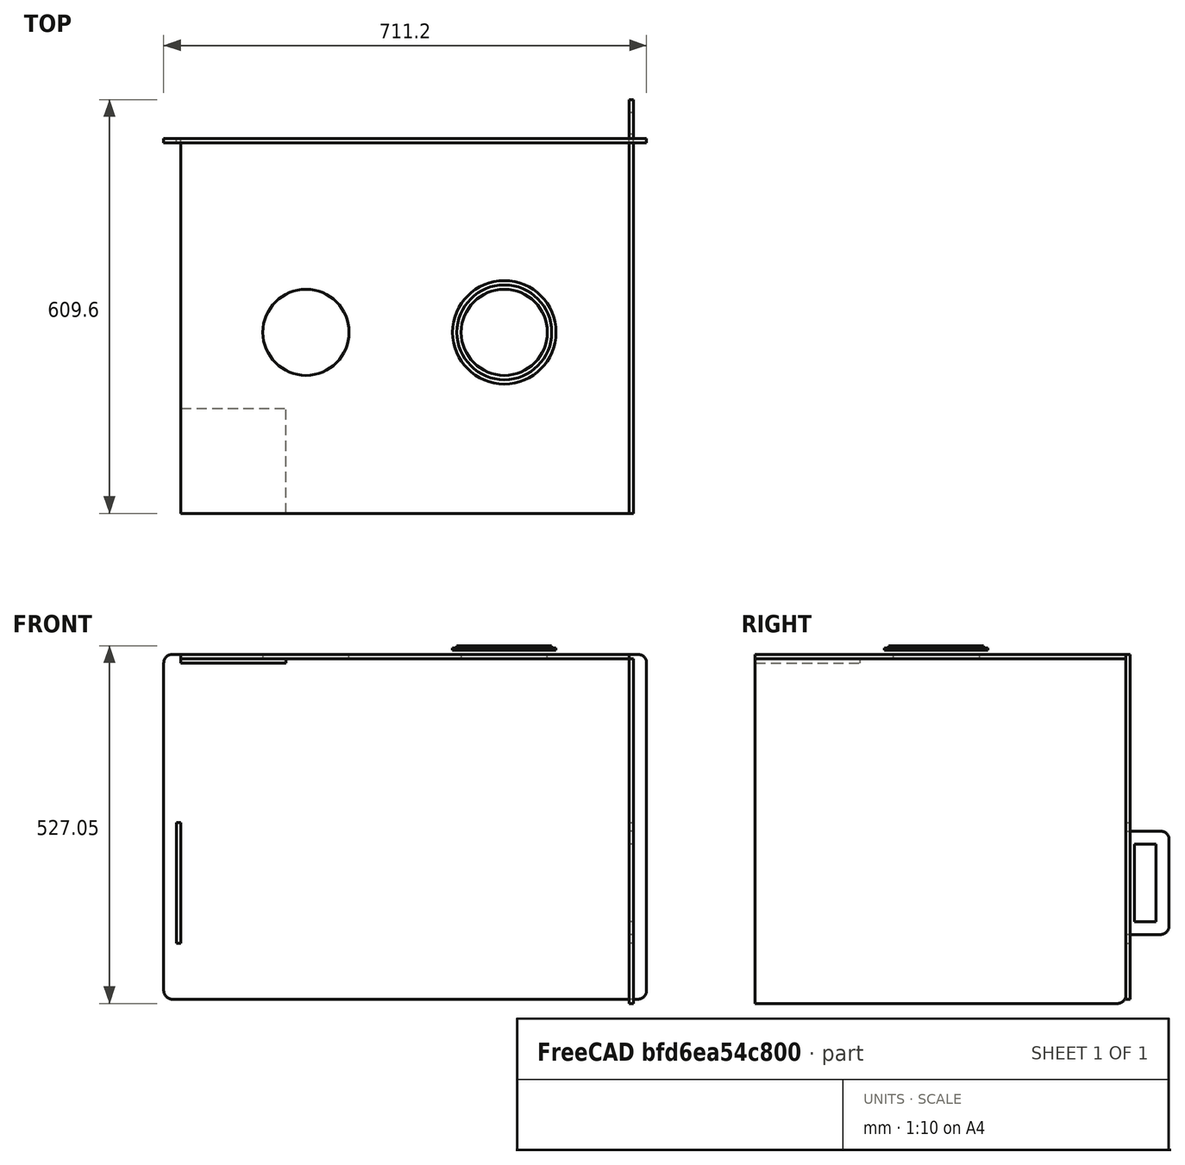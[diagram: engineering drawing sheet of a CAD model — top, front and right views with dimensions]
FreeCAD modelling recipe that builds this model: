
FCSTD DOCUMENT  (FreeCAD 0.19R20364 (Git))
Label: VS_folding_intubation_box
License: All rights reserved
LicenseURL: http://en.wikipedia.org/wiki/All_rights_reserved
objects: TechDraw::DrawViewDimension×28, Sketcher::SketchObject×7, PartDesign::Pad×6, Path::FeaturePython×6, PartDesign::Body×5, TechDraw::DrawSVGTemplate×5, TechDraw::DrawProjGroupItem×5, TechDraw::DrawPage×5, TechDraw::DrawProjGroup×4, TechDraw::DrawRichAnno×3, Part::FeaturePython×2, App::DocumentObjectGroup×2, App::FeaturePython×1, Path::FeatureCompoundPython×1, Part::Feature×1, TechDraw::DrawViewPart×1, Part::Part2DObjectPython×1
note: 31 computed .brp shape members not serialized (recipe doc carries the construction recipe); baked Part::Feature solids carry a one-line shape summary decoded from their .brp

FEATURE [Sketcher::SketchObject] Sketch
  MapMode = 5
  Support = -> [XY_Plane]
  sketch-geometry (7):
    g0: LineSegment StartX=0 StartY=0 StartZ=0 EndX=660.4 EndY=0 EndZ=0
    g1: LineSegment StartX=660.4 StartY=0 StartZ=0 EndX=660.4 EndY=546.1 EndZ=0
    g2: LineSegment StartX=660.4 StartY=546.1 StartZ=0 EndX=0 EndY=546.1 EndZ=0
    g3: LineSegment StartX=0 StartY=546.1 StartZ=0 EndX=0 EndY=0 EndZ=0
    g4: Circle CenterX=184.15 CenterY=266.7 CenterZ=0 NormalX=0 NormalY=0 NormalZ=1 AngleXU=0 Radius=63.5
    g5: Circle CenterX=476.25 CenterY=266.7 CenterZ=0 NormalX=0 NormalY=0 NormalZ=1 AngleXU=0 Radius=63.5
    g6: LineSegment [constr] StartX=660.4 StartY=266.7 StartZ=0 EndX=0 EndY=266.7 EndZ=0
  constraints (22):
    c: Coincident(g0,g1)
    c: Coincident(g1,g2)
    c: Coincident(g2,g3)
    c: Coincident(g3,g0)
    c: Horizontal(g0)
    c: Horizontal(g2)
    c: Vertical(g1)
    c: Vertical(g3)
    c: Coincident(g0,g-1)
    c: DistanceX(g2,g2) = 660.4
    c: DistanceY(g3,g3) = 546.1
    c: Diameter(g4) = 127
    c: Diameter(g5) = 127
    c: DistanceX(g4,g5) = 292.1
    c: DistanceX(g2,g4) = 184.15
    c: DistanceX(g5,g1) = 184.15
    c: PointOnObject(g6,g1)
    c: PointOnObject(g6,g3)
    c: Horizontal(g6)
    c: PointOnObject(g4,g6)
    c: PointOnObject(g5,g6)
    c: DistanceY(g0,g6) = 266.7
FEATURE [PartDesign::Pad] Pad
  Length = 6.35
  Length2 = 99.9998
  Profile = -> Sketch
  Type = 0
FEATURE [PartDesign::Body] Body  label="front"
  Group = -> [Sketch,Pad]
  Origin = -> Origin
  Tip = -> Pad
FEATURE [Sketcher::SketchObject] Sketch001
  MapMode = 5
  Support = -> [XY_Plane001]
  sketch-geometry (16):
    g0: LineSegment StartX=0 StartY=0 StartZ=0 EndX=-508 EndY=0 EndZ=0
    g1: LineSegment StartX=-508 StartY=0 StartZ=0 EndX=-508 EndY=533.4 EndZ=0
    g2: LineSegment StartX=-495.3 StartY=546.1 StartZ=0 EndX=-406.4 EndY=546.1 EndZ=0
    g3: LineSegment StartX=0 StartY=546.1 StartZ=0 EndX=0 EndY=0 EndZ=0
    g4: ArcOfCircle CenterX=-495.3 CenterY=533.4 CenterZ=0 NormalX=0 NormalY=0 NormalZ=1 AngleXU=0 Radius=12.7 StartAngle=1.5708 EndAngle=3.14159
    g5: LineSegment StartX=-254 StartY=546.1 StartZ=0 EndX=-254 EndY=596.9 EndZ=0
    g6: LineSegment StartX=-266.7 StartY=609.6 StartZ=0 EndX=-393.7 EndY=609.6 EndZ=0
    g7: LineSegment StartX=-406.4 StartY=596.9 StartZ=0 EndX=-406.4 EndY=546.1 EndZ=0
    g8: LineSegment StartX=-387.35 StartY=590.55 StartZ=0 EndX=-273.05 EndY=590.55 EndZ=0
    g9: LineSegment StartX=-273.05 StartY=590.55 StartZ=0 EndX=-273.05 EndY=558.8 EndZ=0
    g10: LineSegment StartX=-273.05 StartY=558.8 StartZ=0 EndX=-387.35 EndY=558.8 EndZ=0
    g11: LineSegment StartX=-387.35 StartY=558.8 StartZ=0 EndX=-387.35 EndY=590.55 EndZ=0
    g12: LineSegment StartX=-254 StartY=546.1 StartZ=0 EndX=0 EndY=546.1 EndZ=0
    g13: GeomPoint X=-330.2 Y=609.6 Z=0
    g14: ArcOfCircle CenterX=-266.7 CenterY=596.9 CenterZ=0 NormalX=0 NormalY=0 NormalZ=1 AngleXU=0 Radius=12.7 StartAngle=0 EndAngle=1.5708
    g15: ArcOfCircle CenterX=-393.7 CenterY=596.9 CenterZ=0 NormalX=0 NormalY=0 NormalZ=1 AngleXU=0 Radius=12.7 StartAngle=1.5708 EndAngle=3.14159
  constraints (42):
    c: Coincident(g0,g1)
    c: Coincident(g12,g3)
    c: Coincident(g3,g0)
    c: Horizontal(g0)
    c: Horizontal(g2)
    c: Vertical(g1)
    c: Vertical(g3)
    c: Coincident(g0,g-1)
    c: Tangent(g1,g4) = 1.5708
    c: Tangent(g2,g4) = 1.5708
    c: Radius(g4) = 12.7
    c: DistanceX(g0,g0) = 508
    c: DistanceY(g0,g12) = 546.1
    c: Vertical(g5)
    c: Horizontal(g6)
    c: Vertical(g7)
    c: Coincident(g8,g9)
    c: Coincident(g9,g10)
    c: Coincident(g10,g11)
    c: Coincident(g11,g8)
    c: Horizontal(g8)
    c: Horizontal(g10)
    c: Vertical(g9)
    c: Vertical(g11)
    c: Coincident(g2,g7)
    c: Coincident(g12,g5)
    c: Tangent(g2,g12)
    c: DistanceY(g11,g11) = 31.75
    c: DistanceX(g8,g8) = 114.3
    c: DistanceX(g13,g3) = 330.2
    c: Tangent(g6,g14) = -1.5708
    c: Tangent(g5,g14) = -1.5708
    c: DistanceX(g9,g5) = 19.05
    c: Radius(g14) = 12.7
    c: Tangent(g7,g15) = -1.5708
    c: Tangent(g6,g15) = -1.5708
    c: Radius(g15) = 12.7
    c: DistanceX(g2,g10) = 19.05
    c: DistanceY(g2,g6) = 63.5
    c: DistanceY(g0,g6) = 609.6
    c: Symmetric(g6,g6,g13)
    c: DistanceY(g8,g6) = 19.05
FEATURE [PartDesign::Pad] Pad001
  Length = 6.35
  Length2 = 99.9998
  Profile = -> Sketch001
  Type = 0
FEATURE [PartDesign::Body] Body001  label="left"
  Group = -> [Sketch001,Pad001]
  Origin = -> Origin001
  Placement = pos=(0,0,0) rot=(0,-1,0;1.5708rad)
  Tip = -> Pad001
FEATURE [Sketcher::SketchObject] Sketch002
  MapMode = 5
  Support = -> [XY_Plane002]
  sketch-geometry (19):
    g0: LineSegment StartX=12.7 StartY=-6.35 StartZ=0 EndX=698.5 EndY=-6.35 EndZ=0
    g1: LineSegment StartX=711.2 StartY=6.35 StartZ=0 EndX=711.2 EndY=488.95 EndZ=0
    g2: LineSegment StartX=698.5 StartY=501.65 StartZ=0 EndX=12.7 EndY=501.65 EndZ=0
    g3: LineSegment StartX=0 StartY=488.95 StartZ=0 EndX=0 EndY=6.35 EndZ=0
    g4: LineSegment StartX=692.15 StartY=419.1 StartZ=0 EndX=685.8 EndY=419.1 EndZ=0
    g5: LineSegment StartX=685.8 StartY=419.1 StartZ=0 EndX=685.8 EndY=241.3 EndZ=0
    g6: LineSegment StartX=685.8 StartY=241.3 StartZ=0 EndX=692.15 EndY=241.3 EndZ=0
    g7: LineSegment StartX=692.15 StartY=241.3 StartZ=0 EndX=692.15 EndY=419.1 EndZ=0
    g8: GeomPoint X=692.15 Y=330.2 Z=0
    g9: ArcOfCircle CenterX=698.5 CenterY=488.95 CenterZ=0 NormalX=0 NormalY=0 NormalZ=1 AngleXU=0 Radius=12.7 StartAngle=-9e-16 EndAngle=1.5708
    g10: LineSegment StartX=25.4 StartY=419.1 StartZ=0 EndX=19.05 EndY=419.1 EndZ=0
    g11: LineSegment StartX=19.05 StartY=419.1 StartZ=0 EndX=19.05 EndY=241.3 EndZ=0
    g12: LineSegment StartX=19.05 StartY=241.3 StartZ=0 EndX=25.4 EndY=241.3 EndZ=0
    g13: LineSegment StartX=25.4 StartY=241.3 StartZ=0 EndX=25.4 EndY=419.1 EndZ=0
    g14: GeomPoint X=25.4 Y=330.2 Z=0
    g15: ArcOfCircle CenterX=12.7 CenterY=488.95 CenterZ=0 NormalX=0 NormalY=0 NormalZ=1 AngleXU=0 Radius=12.7 StartAngle=1.5708 EndAngle=3.14159
    g16: ArcOfCircle CenterX=698.5 CenterY=6.35 CenterZ=0 NormalX=0 NormalY=0 NormalZ=1 AngleXU=0 Radius=12.7 StartAngle=4.71239 EndAngle=6.28319
    g17: ArcOfCircle CenterX=12.7 CenterY=6.35 CenterZ=0 NormalX=0 NormalY=0 NormalZ=1 AngleXU=0 Radius=12.7 StartAngle=3.14159 EndAngle=4.71239
    g18: LineSegment [constr] StartX=-26.162 StartY=330.2 StartZ=0 EndX=801.937 EndY=330.2 EndZ=0
  constraints (48):
    c: Horizontal(g0)
    c: Horizontal(g2)
    c: Vertical(g1)
    c: Coincident(g4,g5)
    c: Coincident(g5,g6)
    c: Coincident(g7,g4)
    c: Horizontal(g4)
    c: Horizontal(g6)
    c: Vertical(g5)
    c: Vertical(g7)
    c: DistanceX(g6,g6) = 6.35
    c: Symmetric(g4,g6,g8)
    c: DistanceY(g7,g7) = 177.8
    c: Tangent(g2,g9) = -1.5708
    c: Tangent(g1,g9) = -1.5708
    c: Radius(g9) = 12.7
    c: Coincident(g10,g11)
    c: Coincident(g11,g12)
    c: Coincident(g13,g10)
    c: Horizontal(g10)
    c: Horizontal(g12)
    c: Vertical(g11)
    c: Vertical(g13)
    c: Equal(g6,g12) = 6.35
    c: Symmetric(g10,g12,g14)
    c: Equal(g7,g13) = 177.8
    c: DistanceX(g-1,g12) = 25.4
    c: Tangent(g3,g15) = -1.5708
    c: Tangent(g2,g15) = -1.5708
    c: Radius(g15) = 12.7
    c: Tangent(g0,g16) = -1.5708
    c: Tangent(g1,g16) = -1.5708
    c: DistanceY(g0,g2) = 508
    c: DistanceX(g5,g1) = 25.4
    c: Radius(g16) = 12.7
    c: DistanceX(g3,g1) = 711.2
    c: Tangent(g0,g17) = -1.5708
    c: Tangent(g3,g17) = -1.5708
    c: Radius(g17) = 12.7
    c: DistanceY(g0,g-1) = 6.35
    c: Horizontal(g18)
    c: PointOnObject(g8,g18)
    c: DistanceY(g0,g18) = 336.55
    c: Coincident(g7,g6)
    c: Coincident(g13,g12)
    c: PointOnObject(g14,g18)
    c: Tangent(g3,g-2)
    c: DistanceX(g18,g-1) = 26.162
FEATURE [PartDesign::Pad] Pad002
  Length = 6.35
  Length2 = 99.9998
  Profile = -> Sketch002
  Type = 0
FEATURE [PartDesign::Body] Body002  label="top"
  Group = -> [Sketch002,Pad002]
  Origin = -> Origin002
  Placement = pos=(-25.4,546.1,0) rot=(-1,0,0;1.5708rad)
  Tip = -> Pad002
FEATURE [Sketcher::SketchObject] Sketch003
  MapMode = 5
  Support = -> [XY_Plane003]
  sketch-geometry (2):
    g0: Circle CenterX=0 CenterY=0 CenterZ=0 NormalX=0 NormalY=0 NormalZ=1 AngleXU=0 Radius=63.5
    g1: Circle CenterX=0 CenterY=0 CenterZ=0 NormalX=0 NormalY=0 NormalZ=1 AngleXU=0 Radius=76.2
  constraints (4):
    c: Coincident(g0,g-1)
    c: Coincident(g1,g0)
    c: Diameter(g0) = 127
    c: Diameter(g1) = 152.4
FEATURE [PartDesign::Pad] Pad003
  Length = 3.175
  Length2 = 99.9998
  Profile = -> Sketch003
  Type = 0
FEATURE [Sketcher::SketchObject] Sketch004
  ExternalGeometry = -> [Pad003]
  MapMode = 5
  Placement = pos=(0,0,3.175) rot=(0,0,1;0rad)
  Support = -> [Pad003]
  sketch-geometry (2):
    g0: Circle CenterX=0 CenterY=0 CenterZ=0 NormalX=0 NormalY=0 NormalZ=1 AngleXU=0 Radius=69.85
    g1: Circle CenterX=0 CenterY=0 CenterZ=0 NormalX=0 NormalY=0 NormalZ=1 AngleXU=0 Radius=63.5
  constraints (4):
    c: Coincident(g0,g-1)
    c: Diameter(g0) = 139.7
    c: Coincident(g1,g0)
    c: Diameter(g1) = 127
FEATURE [PartDesign::Pad] Pad004
  BaseFeature = -> Pad003
  Length = 3.175
  Length2 = 99.9998
  Profile = -> Sketch004
  Type = 0
FEATURE [PartDesign::Body] Body003  label="glove_holder"
  Group = -> [Sketch003,Pad003,Sketch004,Pad004]
  Origin = -> Origin003
  Placement = pos=(184.15,266.7,12.7) rot=(1,0,0;0rad)
  Tip = -> Pad004
FEATURE [App::FeaturePython] SetupSheet  # Path/CAM operation (typed FeaturePython)
  ClearanceHeightExpression = OpStockZMax+SetupSheet.ClearanceHeightOffset
  ClearanceHeightOffset = 5.0038
  CoolantMode = 0
  CoolantModes = None | Flood | Mist
  FinalDepthExpression = OpFinalDepth
  HorizRapid = 0
  SafeHeightExpression = OpStockZMax+SetupSheet.SafeHeightOffset
  SafeHeightOffset = 2.9972
  StartDepthExpression = OpStartDepth
  StepDownExpression = OpToolDiameter
  VertRapid = 0
FEATURE [Part::FeaturePython] Clone  label="Model-glove_holder"  # Draft clone (typed FeaturePython)
  AttacherType = Attacher::AttachEngine3D
  Fuse = false
  Objects = -> [Body003]
  PathResource = Model
  Placement = pos=(76.9435,77.1288,-6.35) rot=(1,0,0;0rad)
  Scale = (1,1,1)
FEATURE [App::DocumentObjectGroup] Model
  Group = -> [Clone]
FEATURE [Path::FeaturePython] Default_Tool  label="Default Tool"  # Path/CAM operation (typed FeaturePython)
  HorizFeed = 0
  HorizRapid = 0
  SpindleDir = 0
  SpindleSpeed = 0
  ToolNumber = 1
  VertFeed = 0
  VertRapid = 0
  expr: VertRapid = SetupSheet.VertRapid
  expr: HorizRapid = SetupSheet.HorizRapid
FEATURE [Part::FeaturePython] Stock  # WARN: FeaturePython — macro-defined, semantics opaque (R4)
  Base = -> Model
  ExtXneg = 0.9906
  ExtXpos = 0.9906
  ExtYneg = 0.9906
  ExtYpos = 0.9906
  ExtZneg = 0
  ExtZpos = 0
  Placement = pos=(0.9906,0.9906,-6.35) rot=(0,0,1;0rad)
  StockType = FromBase
FEATURE [Path::FeaturePython] T5__1_8_endmill  label="T5: 1/8 endmill"  # Path/CAM operation (typed FeaturePython)
  HorizFeed = 19.05
  HorizRapid = 0
  SpindleDir = 0
  SpindleSpeed = 20000
  ToolNumber = 5
  VertFeed = 8.46667
  VertRapid = 0
  expr: VertRapid = SetupSheet.VertRapid
  expr: HorizRapid = SetupSheet.HorizRapid
FEATURE [Path::FeaturePython] Profile_Edges  # Path/CAM operation (typed FeaturePython)
  Active = true
  AreaParams:
    Tolerance = 1e-07
    FitArcs = True
    Simplify = False
    CleanDistance = 0.0
    Accuracy = 0.01
    Unit = 1.0
    MinArcPoints = 4
    MaxArcPoints = 100
    ClipperScale = 10000000.0
    Fill = 0
    Coplanar = 0
    Reorient = True
    Outline = False
    Explode = False
    OpenMode = 0
    Deflection = 0.01
    SubjectFill = 0
    ClipFill = 0
    Offset = -1.5875
    ExtraPass = 0
    Stepover = 0.0
    LastStepover = 0.0
    JoinType = 0
    EndType = 0
    MiterLimit = 2.0
    RoundPrecision = 0.0
    PocketMode = 0
    ToolRadius = 1.0
    PocketExtraOffset = 0.0
    PocketStepover = 0.0
    PocketLastStepover = 0.0
    FromCenter = False
    Angle = 45.0
    AngleShift = 0.0
    Shift = 0.0
    Thicken = False
    SectionCount = -1
    Stepdown = 1.0
    SectionOffset = 0.0
    SectionTolerance = 1e-06
    SectionMode = 2
    Project = False
  Base = -> [Clone]
  ClearanceHeight = 5.0038
  CoolantMode = None
  Direction = 0
  EnableRotation = 0
  FinalDepth = -6.4008
  JoinType = 0
  MiterLimit = 0.1
  OffsetExtra = 0
  OpFinalDepth = -6.35
  OpStartDepth = 0
  OpStockZMax = 0
  OpStockZMin = -6.35
  OpToolDiameter = 3.175
  PathParams = {'orientation': 1, 'feedrate': 19.05, 'feedrate_v': 8.46667, 'verbose': True, 'resume_height': 2.9972, 'retraction': 5.0038, 'return_end': True, 'preamble': False}
  SafeHeight = 2.9972
  Side = 1
  StartDepth = 0
  StartPoint = (0,0,0)
  StepDown = 3.2004
  ToolController = -> T5__1_8_endmill
  UseComp = true
  UseStartPoint = false
  expr: StartDepth = OpStartDepth
  expr: FinalDepth = -0.252in
  expr: StepDown = 0.126in
  expr: SafeHeight = OpStockZMax + SetupSheet.SafeHeightOffset
  expr: ClearanceHeight = OpStockZMax + SetupSheet.ClearanceHeightOffset
FEATURE [Path::FeaturePython] Pocket_Shape  # Path/CAM operation (typed FeaturePython)
  Active = true
  AreaParams:
    Tolerance = 1e-07
    FitArcs = True
    Simplify = False
    CleanDistance = 0.0
    Accuracy = 0.01
    Unit = 1.0
    MinArcPoints = 4
    MaxArcPoints = 100
    ClipperScale = 10000000.0
    Fill = 0
    Coplanar = 0
    Reorient = True
    Outline = False
    Explode = False
    OpenMode = 0
    Deflection = 0.01
    SubjectFill = 0
    ClipFill = 0
    Offset = 0.0
    ExtraPass = 0
    Stepover = 0.0
    LastStepover = 0.0
    JoinType = 0
    EndType = 0
    MiterLimit = 2.0
    RoundPrecision = 0.0
    PocketMode = 3
    ToolRadius = 1.5875
    PocketExtraOffset = 0.254
    PocketStepover = 2.54
    PocketLastStepover = 0.0
    FromCenter = True
    Angle = 45.0
    AngleShift = 0.0
    Shift = 0.0
    Thicken = False
    SectionCount = -1
    Stepdown = 1.0
    SectionOffset = 0.0
    SectionTolerance = 1e-06
    SectionMode = 2
    Project = False
  AttemptInverseAngle = true
  Base = -> [Clone]
  ClearanceHeight = 5.0038
  CoolantMode = None
  CutMode = 0
  EnableRotation = 0
  ExtensionCorners = true
  ExtensionLengthDefault = 1.5875
  ExtraOffset = 0.254
  FinalDepth = -3.175
  FinishDepth = 0
  InverseAngle = false
  KeepToolDown = false
  LimitDepthToFace = true
  MinTravel = false
  OffsetPattern = 2
  OpFinalDepth = -3.175
  OpStartDepth = 0
  OpStockZMax = 0
  OpStockZMin = -6.35
  OpToolDiameter = 3.175
  PathParams = {'orientation': 1, 'feedrate': 19.05, 'feedrate_v': 8.46667, 'verbose': True, 'resume_height': 2.9972, 'retraction': 5.0038, 'return_end': True, 'preamble': False}
  ReverseDirection = false
  SafeHeight = 2.9972
  StartAt = 0
  StartDepth = 0
  StartPoint = (0,0,0)
  StepDown = 3.175
  StepOver = 80
  ToolController = -> T5__1_8_endmill
  UseOutline = false
  UseStartPoint = false
  ZigZagAngle = 45
  expr: StartDepth = OpStartDepth
  expr: FinalDepth = OpFinalDepth
  expr: StepDown = OpToolDiameter
  expr: SafeHeight = OpStockZMax + SetupSheet.SafeHeightOffset
  expr: ClearanceHeight = OpStockZMax + SetupSheet.ClearanceHeightOffset
  expr: ExtensionLengthDefault = OpToolDiameter / 2
FEATURE [Path::FeaturePython] Contour  # Path/CAM operation (typed FeaturePython)
  Active = true
  AreaParams:
    Tolerance = 1e-07
    FitArcs = True
    Simplify = False
    CleanDistance = 0.0
    Accuracy = 0.01
    Unit = 1.0
    MinArcPoints = 4
    MaxArcPoints = 100
    ClipperScale = 10000000.0
    Fill = 0
    Coplanar = 2
    Reorient = True
    Outline = False
    Explode = False
    OpenMode = 0
    Deflection = 0.01
    SubjectFill = 0
    ClipFill = 0
    Offset = 1.5875
    ExtraPass = 0
    Stepover = 0.0
    LastStepover = 0.0
    JoinType = 0
    EndType = 0
    MiterLimit = 2.0
    RoundPrecision = 0.0
    PocketMode = 0
    ToolRadius = 1.0
    PocketExtraOffset = 0.0
    PocketStepover = 0.0
    PocketLastStepover = 0.0
    FromCenter = False
    Angle = 45.0
    AngleShift = 0.0
    Shift = 0.0
    Thicken = False
    SectionCount = -1
    Stepdown = 1.0
    SectionOffset = 0.0
    SectionTolerance = 1e-06
    SectionMode = 2
    Project = False
  ClearanceHeight = 5.0038
  CoolantMode = None
  Direction = 0
  EnableRotation = 0
  FinalDepth = -6.4008
  JoinType = 0
  MiterLimit = 0.1
  OffsetExtra = 0
  OpFinalDepth = -6.35
  OpStartDepth = 0
  OpStockZMax = 0
  OpStockZMin = -6.35
  OpToolDiameter = 3.175
  PathParams = {'orientation': 1, 'feedrate': 19.05, 'feedrate_v': 8.46667, 'verbose': True, 'resume_height': 2.9972, 'retraction': 5.0038, 'return_end': True, 'preamble': False}
  SafeHeight = 2.9972
  Side = 0
  StartDepth = 0
  StartPoint = (0,0,0)
  StepDown = 3.2004
  ToolController = -> T5__1_8_endmill
  UseComp = true
  UseStartPoint = false
  expr: StartDepth = OpStartDepth
  expr: FinalDepth = -0.252in
  expr: StepDown = 0.126in
  expr: SafeHeight = OpStockZMax + SetupSheet.SafeHeightOffset
  expr: ClearanceHeight = OpStockZMax + SetupSheet.ClearanceHeightOffset
FEATURE [Path::FeatureCompoundPython] Operations  # Path/CAM operation (typed FeaturePython)
  Group = -> [Pocket_Shape,Profile_Edges,Contour]
  UsePlacements = false
FEATURE [Path::FeaturePython] Job  # Path/CAM operation (typed FeaturePython)
  Fixtures = G54
  GeometryTolerance = 0
  Model = -> Model
  Operations = -> Operations
  OrderOutputBy = 0
  PostProcessor = 1
  SetupSheet = -> SetupSheet
  SplitOutput = false
  Stock = -> Stock
  ToolController = -> [Default_Tool,T5__1_8_endmill]
FEATURE [TechDraw::DrawSVGTemplate] Template
  EditableTexts = Designed_by_Name=Adam Spontarelli; Drawing_number=2 of 5; FC-Date=4/14/2020; FC-SC=Scale; FC-Title=Folding Intubation Box; Subtitle=Front Panel
  Height = 215.9
  Orientation = 1
  Width = 279.4
FEATURE [TechDraw::DrawProjGroupItem] ProjItem  label="Front"
  CoarseView = false
  Direction = (0,0,1)
  Focus = 100
  HardHidden = true
  IsoCount = 0
  IsoHidden = false
  IsoVisible = false
  LockPosition = true
  Perspective = false
  Rotation = 0
  RotationVector = (1,0,0)
  Scale = 0.2
  ScaleType = 2
  SeamHidden = false
  SeamVisible = true
  SmoothHidden = false
  SmoothVisible = true
  Source = -> [Body]
  Type = 0
  X = 0
  XDirection = (1,0,0)
  Y = 0
FEATURE [TechDraw::DrawProjGroup] ProjGroup
  Anchor = -> ProjItem
  AutoDistribute = true
  LockPosition = false
  ProjectionType = 0
  Rotation = 0
  Scale = 0.2
  ScaleType = 1
  Source = -> [Body]
  Views = -> [ProjItem]
  X = 138.242
  Y = 130.544
  spacingX = 15
  spacingY = 15
FEATURE [TechDraw::DrawViewDimension] Dimension
  Arbitrary = false
  FormatSpec = ⌀%.4f
  Inverted = false
  LockPosition = false
  MeasureType = 1
  OverTolerance = 0
  References2D = -> [ProjItem]
  Rotation = 0
  ScaleType = 1
  TheoreticalExact = false
  Type = 5
  UnderTolerance = 0
  X = -0.728834
  Y = 14.5767
FEATURE [TechDraw::DrawViewDimension] Dimension001
  Arbitrary = false
  FormatSpec = %.4f
  Inverted = false
  LockPosition = false
  MeasureType = 1
  OverTolerance = 0
  References2D = -> [ProjItem]
  Rotation = 0
  ScaleType = 1
  TheoreticalExact = false
  Type = 1
  UnderTolerance = 0
  X = 0
  Y = 4.91417
FEATURE [TechDraw::DrawViewDimension] Dimension002
  Arbitrary = false
  FormatSpec = %.4f
  Inverted = false
  LockPosition = false
  MeasureType = 1
  OverTolerance = 0
  References2D = -> [ProjItem]
  Rotation = 0
  ScaleType = 1
  TheoreticalExact = false
  Type = 1
  UnderTolerance = 0
  X = -49.4471
  Y = 4.66986
FEATURE [TechDraw::DrawViewDimension] Dimension003
  Arbitrary = false
  FormatSpec = %.4f
  Inverted = false
  LockPosition = false
  MeasureType = 1
  OverTolerance = 0
  References2D = -> [ProjItem]
  Rotation = 0
  ScaleType = 1
  TheoreticalExact = false
  Type = 2
  UnderTolerance = 0
  X = -5.71705
  Y = -25.9412
FEATURE [TechDraw::DrawViewDimension] Dimension004
  Arbitrary = false
  FormatSpec = %.4f
  Inverted = false
  LockPosition = false
  MeasureType = 1
  OverTolerance = 0
  References2D = -> [ProjItem]
  Rotation = 0
  ScaleType = 1
  TheoreticalExact = false
  Type = 2
  UnderTolerance = 0
  X = 72.5995
  Y = 2.55092
FEATURE [TechDraw::DrawViewDimension] Dimension005
  Arbitrary = false
  FormatSpec = %.4f
  Inverted = false
  LockPosition = false
  MeasureType = 1
  OverTolerance = 0
  References2D = -> [ProjItem]
  Rotation = 0
  ScaleType = 1
  TheoreticalExact = false
  Type = 1
  UnderTolerance = 0
  X = -1.45767
  Y = 64.8137
FEATURE [TechDraw::DrawPage] Page  label="front001"
  KeepUpdated = true
  NextBalloonIndex = 1
  ProjectionType = 0
  Template = -> Template
  Views = -> [ProjGroup,Dimension,Dimension001,Dimension002,Dimension003,Dimension004,Dimension005]
FEATURE [TechDraw::DrawSVGTemplate] Template001
  EditableTexts = Designed_by_Name=Adam Spontarelli; Drawing_number=3 of 5; FC-Date=4/14/2020; FC-SC=Scale; FC-Title=Folding Intubation Box; Subtitle=Side Panel
  Height = 215.9
  Orientation = 1
  Width = 279.4
FEATURE [TechDraw::DrawProjGroupItem] ProjItem001  label="Front001"
  CoarseView = false
  Direction = (-1,0,0)
  Focus = 100
  HardHidden = true
  IsoCount = 0
  IsoHidden = false
  IsoVisible = false
  LockPosition = true
  Perspective = false
  Rotation = 0
  RotationVector = (0,0,1)
  Scale = 0.2
  ScaleType = 2
  SeamHidden = false
  SeamVisible = true
  SmoothHidden = false
  SmoothVisible = true
  Source = -> [Body001]
  Type = 0
  X = 0
  XDirection = (0,0,1)
  Y = 0
FEATURE [TechDraw::DrawProjGroup] ProjGroup001
  Anchor = -> ProjItem001
  AutoDistribute = true
  LockPosition = false
  ProjectionType = 0
  Rotation = 0
  Scale = 0.2
  ScaleType = 1
  Source = -> [Body001]
  Views = -> [ProjItem001]
  X = 140.033
  Y = 134.563
  spacingX = 15
  spacingY = 15
FEATURE [TechDraw::DrawViewDimension] Dimension006
  Arbitrary = false
  FormatSpec = %.4f
  Inverted = false
  LockPosition = false
  MeasureType = 1
  OverTolerance = 0
  References2D = -> [ProjItem001]
  Rotation = 0
  ScaleType = 1
  TheoreticalExact = false
  Type = 1
  UnderTolerance = 0
  X = -1.66333
  Y = -67.6133
FEATURE [TechDraw::DrawViewDimension] Dimension007
  Arbitrary = false
  FormatSpec = %.4f
  Inverted = false
  LockPosition = false
  MeasureType = 1
  OverTolerance = 0
  References2D = -> [ProjItem001]
  Rotation = 0
  ScaleType = 1
  TheoreticalExact = false
  Type = 2
  UnderTolerance = 0
  X = 55.4573
  Y = -6.35
FEATURE [TechDraw::DrawViewDimension] Dimension008
  Arbitrary = false
  FormatSpec = %.4f
  Inverted = false
  LockPosition = false
  MeasureType = 1
  OverTolerance = 0
  References2D = -> [ProjItem001]
  Rotation = 0
  ScaleType = 1
  TheoreticalExact = false
  Type = 1
  UnderTolerance = 0
  X = -16.9974
  Y = 42.5987
FEATURE [TechDraw::DrawViewDimension] Dimension009
  Arbitrary = false
  FormatSpec = %.4f
  Inverted = false
  LockPosition = false
  MeasureType = 1
  OverTolerance = 0
  References2D = -> [ProjItem001]
  Rotation = 0
  ScaleType = 1
  TheoreticalExact = false
  Type = 1
  UnderTolerance = 0
  X = 23.0568
  Y = 42.6949
FEATURE [TechDraw::DrawViewDimension] Dimension010
  Arbitrary = false
  FormatSpec = %.4f
  Inverted = false
  LockPosition = false
  MeasureType = 1
  OverTolerance = 0
  References2D = -> [ProjItem001]
  Rotation = 0
  ScaleType = 1
  TheoreticalExact = false
  Type = 1
  UnderTolerance = 0
  X = 7.76077
  Y = 32.8346
FEATURE [TechDraw::DrawViewDimension] Dimension011
  Arbitrary = false
  FormatSpec = %.4f
  Inverted = false
  LockPosition = false
  MeasureType = 1
  OverTolerance = 0
  References2D = -> [ProjItem001]
  Rotation = 0
  ScaleType = 1
  TheoreticalExact = false
  Type = 2
  UnderTolerance = 0
  X = 4.53771
  Y = 57.2976
FEATURE [TechDraw::DrawViewDimension] Dimension012
  Arbitrary = false
  FormatSpec = %.4f
  Inverted = false
  LockPosition = false
  MeasureType = 1
  OverTolerance = 0
  References2D = -> [ProjItem001]
  Rotation = 0
  ScaleType = 1
  TheoreticalExact = false
  Type = 1
  UnderTolerance = 0
  X = -14.9471
  Y = 22.924
FEATURE [TechDraw::DrawViewDimension] Dimension013
  Arbitrary = false
  FormatSpec = R%.4f
  Inverted = false
  LockPosition = false
  MeasureType = 1
  OverTolerance = 0
  References2D = -> [ProjItem001]
  Rotation = 0
  ScaleType = 1
  TheoreticalExact = false
  Type = 4
  UnderTolerance = 0
  X = -40.9578
  Y = 41.3359
FEATURE [TechDraw::DrawSVGTemplate] Template002
  EditableTexts = Designed_by_Name=Adam Spontarelli; Drawing_number=4 of 5; FC-Date=4/14/2020; FC-SC=Scale; FC-Title=Folding Intubation Box; Subtitle=Top Panel
  Height = 215.9
  Orientation = 1
  Width = 279.4
FEATURE [TechDraw::DrawProjGroupItem] ProjItem002  label="Front002"
  CoarseView = false
  Direction = (0,1,0)
  Focus = 100
  HardHidden = true
  IsoCount = 0
  IsoHidden = false
  IsoVisible = false
  LockPosition = true
  Perspective = false
  Rotation = 0
  RotationVector = (1,0,0)
  Scale = 0.2
  ScaleType = 2
  SeamHidden = false
  SeamVisible = true
  SmoothHidden = false
  SmoothVisible = true
  Source = -> [Body002]
  Type = 0
  X = 0
  XDirection = (1,0,0)
  Y = 0
FEATURE [TechDraw::DrawProjGroup] ProjGroup002
  Anchor = -> ProjItem002
  AutoDistribute = true
  LockPosition = false
  ProjectionType = 0
  Rotation = 0
  Scale = 0.2
  ScaleType = 1
  Source = -> [Body002]
  Views = -> [ProjItem002]
  X = 141.363
  Y = 131.902
  spacingX = 15
  spacingY = 15
FEATURE [TechDraw::DrawViewDimension] Dimension014
  Arbitrary = false
  FormatSpec = %.4f
  Inverted = false
  LockPosition = false
  MeasureType = 1
  OverTolerance = 0
  References2D = -> [ProjItem002]
  Rotation = 0
  ScaleType = 1
  TheoreticalExact = false
  Type = 1
  UnderTolerance = 0
  X = 92.3109
  Y = 41.6325
FEATURE [TechDraw::DrawViewDimension] Dimension015
  Arbitrary = false
  FormatSpec = %.4f
  Inverted = false
  LockPosition = false
  MeasureType = 1
  OverTolerance = 0
  References2D = -> [ProjItem002]
  Rotation = 0
  ScaleType = 1
  TheoreticalExact = false
  Type = 2
  UnderTolerance = 0
  X = -53.8461
  Y = 16.4733
FEATURE [TechDraw::DrawViewDimension] Dimension018
  Arbitrary = false
  FormatSpec = %.4f
  Inverted = false
  LockPosition = false
  MeasureType = 1
  OverTolerance = 0
  References2D = -> [ProjItem002]
  Rotation = 0
  ScaleType = 1
  TheoreticalExact = false
  Type = 1
  UnderTolerance = 0
  X = -4.85889
  Y = 62.2293
FEATURE [TechDraw::DrawViewDimension] Dimension019
  Arbitrary = false
  FormatSpec = %.4f
  Inverted = false
  LockPosition = false
  MeasureType = 1
  OverTolerance = 0
  References2D = -> [ProjItem002]
  Rotation = 0
  ScaleType = 1
  TheoreticalExact = false
  Type = 2
  UnderTolerance = 0
  X = 76.7794
  Y = 6.68098
FEATURE [TechDraw::DrawViewDimension] Dimension020
  Arbitrary = false
  FormatSpec = R%.4f
  Inverted = false
  LockPosition = false
  MeasureType = 1
  OverTolerance = 0
  References2D = -> [ProjItem002]
  Rotation = 0
  ScaleType = 1
  TheoreticalExact = false
  Type = 4
  UnderTolerance = 0
  X = -63.4693
  Y = -38.2638
FEATURE [TechDraw::DrawViewDimension] Dimension021
  Arbitrary = false
  FormatSpec = %.4f
  Inverted = false
  LockPosition = false
  MeasureType = 1
  OverTolerance = 0
  References2D = -> [ProjItem002]
  Rotation = 0
  ScaleType = 1
  TheoreticalExact = false
  Type = 2
  UnderTolerance = 0
  X = 1.00364
  Y = -19.52
FEATURE [TechDraw::DrawViewDimension] Dimension022
  Arbitrary = false
  FormatSpec = %.4f
  Inverted = false
  LockPosition = false
  MeasureType = 1
  OverTolerance = 0
  References2D = -> [ProjItem002]
  Rotation = 0
  ScaleType = 1
  TheoreticalExact = false
  Type = 2
  UnderTolerance = 0
  X = 47.3392
  Y = 42.3577
FEATURE [TechDraw::DrawSVGTemplate] Template003
  EditableTexts = Designed_by_Name=Adam Spontarelli; Drawing_number=5 of 5; FC-Date=4/14/2020; FC-SC=Scale; FC-Title=Folding Intubation Box; Subtitle=Glove Flange
  Height = 215.9
  Orientation = 1
  Width = 279.4
FEATURE [TechDraw::DrawProjGroupItem] ProjItem003  label="Front003"
  CoarseView = false
  Direction = (0,0,1)
  Focus = 100
  HardHidden = true
  IsoCount = 0
  IsoHidden = false
  IsoVisible = false
  LockPosition = true
  Perspective = false
  Rotation = 0
  RotationVector = (1,0,0)
  Scale = 0.75
  ScaleType = 2
  SeamHidden = false
  SeamVisible = true
  SmoothHidden = false
  SmoothVisible = true
  Source = -> [Body003]
  Type = 0
  X = 0
  XDirection = (1,0,0)
  Y = 0
FEATURE [TechDraw::DrawProjGroupItem] ProjItem004  label="Bottom"
  CoarseView = false
  Direction = (0,-1,0)
  Focus = 100
  HardHidden = true
  IsoCount = 0
  IsoHidden = false
  IsoVisible = false
  LockPosition = true
  Perspective = false
  Rotation = 0
  RotationVector = (1,0,0)
  Scale = 0.75
  ScaleType = 2
  SeamHidden = false
  SeamVisible = true
  SmoothHidden = false
  SmoothVisible = true
  Source = -> [Body003]
  Type = 5
  X = 0
  XDirection = (1,0,0)
  Y = 81.2605
FEATURE [TechDraw::DrawProjGroup] ProjGroup003
  Anchor = -> ProjItem003
  AutoDistribute = true
  LockPosition = false
  ProjectionType = 0
  Rotation = 0
  Scale = 0.75
  ScaleType = 2
  Source = -> [Body003]
  Views = -> [ProjItem003,ProjItem004]
  X = 86.2393
  Y = 101.052
  spacingX = 15
  spacingY = 15
FEATURE [TechDraw::DrawViewDimension] Dimension023
  Arbitrary = false
  FormatSpec = ⌀%.4f
  Inverted = false
  LockPosition = false
  MeasureType = 1
  OverTolerance = 0
  References2D = -> [ProjItem003]
  Rotation = 0
  ScaleType = 1
  TheoreticalExact = false
  Type = 5
  UnderTolerance = 0
  X = 27.9994
  Y = 4.43554
FEATURE [TechDraw::DrawViewDimension] Dimension024
  Arbitrary = false
  FormatSpec = ⌀%.4f
  Inverted = false
  LockPosition = false
  MeasureType = 1
  OverTolerance = 0
  References2D = -> [ProjItem003]
  Rotation = 0
  ScaleType = 1
  TheoreticalExact = false
  Type = 5
  UnderTolerance = 0
  X = 27.9994
  Y = 12.7522
FEATURE [TechDraw::DrawViewDimension] Dimension025
  Arbitrary = false
  FormatSpec = ⌀%.4f
  Inverted = false
  LockPosition = false
  MeasureType = 1
  OverTolerance = 0
  References2D = -> [ProjItem003]
  Rotation = 0
  ScaleType = 1
  TheoreticalExact = false
  Type = 5
  UnderTolerance = 0
  X = 59.8798
  Y = 37.7021
FEATURE [TechDraw::DrawViewDimension] Dimension026
  Arbitrary = false
  FormatSpec = %.4f
  Inverted = false
  LockPosition = false
  MeasureType = 1
  OverTolerance = 0
  References2D = -> [ProjItem004]
  Rotation = 0
  ScaleType = 1
  TheoreticalExact = false
  Type = 2
  UnderTolerance = 0
  X = 56.9235
  Y = 10.6806
FEATURE [TechDraw::DrawViewDimension] Dimension027
  Arbitrary = false
  FormatSpec = %.4f
  Inverted = false
  LockPosition = false
  MeasureType = 1
  OverTolerance = 0
  References2D = -> [ProjItem004]
  Rotation = 0
  ScaleType = 1
  TheoreticalExact = false
  Type = 2
  UnderTolerance = 0
  X = 62.598
  Y = -12.9653
FEATURE [TechDraw::DrawSVGTemplate] Template004
  EditableTexts = Designed_by_Name=Adam Spontarelli; Drawing_number=1 of 5; FC-Date=4/15/2020; FC-SC=Scale; FC-Title=Folding Intubation Box; Subtitle=Assembly
  Height = 215.9
  Orientation = 1
  Width = 279.4
FEATURE [Sketcher::SketchObject] Sketch005
  MapMode = 5
  Support = -> [XY_Plane004]
  sketch-geometry (16):
    g0: LineSegment StartX=0 StartY=0 StartZ=0 EndX=-508 EndY=0 EndZ=0
    g1: LineSegment StartX=-508 StartY=0 StartZ=0 EndX=-508 EndY=533.4 EndZ=0
    g2: LineSegment StartX=-495.3 StartY=546.1 StartZ=0 EndX=-406.4 EndY=546.1 EndZ=0
    g3: LineSegment StartX=0 StartY=546.1 StartZ=0 EndX=0 EndY=0 EndZ=0
    g4: ArcOfCircle CenterX=-495.3 CenterY=533.4 CenterZ=0 NormalX=0 NormalY=0 NormalZ=1 AngleXU=0 Radius=12.7 StartAngle=1.5708 EndAngle=3.14159
    g5: LineSegment StartX=-254 StartY=546.1 StartZ=0 EndX=-254 EndY=596.9 EndZ=0
    g6: LineSegment StartX=-266.7 StartY=609.6 StartZ=0 EndX=-393.7 EndY=609.6 EndZ=0
    g7: LineSegment StartX=-406.4 StartY=596.9 StartZ=0 EndX=-406.4 EndY=546.1 EndZ=0
    g8: LineSegment StartX=-387.35 StartY=590.55 StartZ=0 EndX=-273.05 EndY=590.55 EndZ=0
    g9: LineSegment StartX=-273.05 StartY=590.55 StartZ=0 EndX=-273.05 EndY=558.8 EndZ=0
    g10: LineSegment StartX=-273.05 StartY=558.8 StartZ=0 EndX=-387.35 EndY=558.8 EndZ=0
    g11: LineSegment StartX=-387.35 StartY=558.8 StartZ=0 EndX=-387.35 EndY=590.55 EndZ=0
    g12: LineSegment StartX=-254 StartY=546.1 StartZ=0 EndX=0 EndY=546.1 EndZ=0
    g13: GeomPoint X=-330.2 Y=609.6 Z=0
    g14: ArcOfCircle CenterX=-266.7 CenterY=596.9 CenterZ=0 NormalX=0 NormalY=0 NormalZ=1 AngleXU=0 Radius=12.7 StartAngle=0 EndAngle=1.5708
    g15: ArcOfCircle CenterX=-393.7 CenterY=596.9 CenterZ=0 NormalX=0 NormalY=0 NormalZ=1 AngleXU=0 Radius=12.7 StartAngle=1.5708 EndAngle=3.14159
  constraints (42):
    c: Coincident(g0,g1)
    c: Coincident(g12,g3)
    c: Coincident(g3,g0)
    c: Horizontal(g0)
    c: Horizontal(g2)
    c: Vertical(g1)
    c: Vertical(g3)
    c: Coincident(g0,g-1)
    c: Tangent(g1,g4) = 1.5708
    c: Tangent(g2,g4) = 1.5708
    c: Radius(g4) = 12.7
    c: DistanceX(g0,g0) = 508
    c: DistanceY(g0,g12) = 546.1
    c: Vertical(g5)
    c: Horizontal(g6)
    c: Vertical(g7)
    c: Coincident(g8,g9)
    c: Coincident(g9,g10)
    c: Coincident(g10,g11)
    c: Coincident(g11,g8)
    c: Horizontal(g8)
    c: Horizontal(g10)
    c: Vertical(g9)
    c: Vertical(g11)
    c: Coincident(g2,g7)
    c: Coincident(g12,g5)
    c: Tangent(g2,g12)
    c: DistanceY(g11,g11) = 31.75
    c: DistanceX(g8,g8) = 114.3
    c: DistanceX(g13,g3) = 330.2
    c: Tangent(g6,g14) = -1.5708
    c: Tangent(g5,g14) = -1.5708
    c: DistanceX(g9,g5) = 19.05
    c: Radius(g14) = 12.7
    c: Tangent(g7,g15) = -1.5708
    c: Tangent(g6,g15) = -1.5708
    c: Radius(g15) = 12.7
    c: DistanceX(g2,g10) = 19.05
    c: DistanceY(g2,g6) = 63.5
    c: DistanceY(g0,g6) = 609.6
    c: Symmetric(g6,g6,g13)
    c: DistanceY(g8,g6) = 19.05
FEATURE [PartDesign::Pad] Pad005
  Length = 6.35
  Length2 = 99.9998
  Profile = -> Sketch005
  Type = 0
FEATURE [PartDesign::Body] Body004  label="right"
  Group = -> [Sketch005,Pad005]
  Origin = -> Origin004
  Placement = pos=(666.75,0,0) rot=(0,-1,0;1.5708rad)
  Tip = -> Pad005
FEATURE [Part::Feature] Body003001  label="glove_holder2"
  Placement = pos=(476.25,266.7,12.7) rot=(0,0,1;0rad)
  shape: bbox 152.4 x 152.4 x 6.35 mm, 7 faces (baked)
FEATURE [TechDraw::DrawViewPart] View
  CoarseView = false
  Direction = (-0.637,0.28,0.718)
  Focus = 100
  HardHidden = false
  IsoCount = 0
  IsoHidden = false
  IsoVisible = false
  LockPosition = false
  Perspective = false
  Rotation = 0
  Scale = 0.16
  ScaleType = 0
  SeamHidden = false
  SeamVisible = true
  SmoothHidden = false
  SmoothVisible = true
  Source = -> [Body003001,Body004,Body003,Body002,Body001,Body]
  X = 119.843
  XDirection = (0.749,0.006,0.662)
  Y = 131.056
FEATURE [TechDraw::DrawViewDimension] Dimension028
  Arbitrary = false
  FormatSpec = %.4f
  Inverted = false
  LockPosition = false
  MeasureType = 1
  OverTolerance = 0
  References2D = -> [ProjItem002]
  Rotation = 0
  ScaleType = 0
  TheoreticalExact = false
  Type = 1
  UnderTolerance = 0
  X = -53.0354
  Y = -10.474
FEATURE [TechDraw::DrawViewDimension] Dimension029
  Arbitrary = false
  FormatSpec = %.4f
  Inverted = false
  LockPosition = false
  MeasureType = 1
  OverTolerance = 0
  References2D = -> [ProjItem002]
  Rotation = 0
  ScaleType = 0
  TheoreticalExact = false
  Type = 1
  UnderTolerance = 0
  X = 55.7933
  Y = -6.21172
FEATURE [TechDraw::DrawPage] Page002  label="top001"
  KeepUpdated = true
  NextBalloonIndex = 1
  ProjectionType = 0
  Template = -> Template002
  Views = -> [ProjGroup002,Dimension014,Dimension015,Dimension018,Dimension019,Dimension020,Dimension021,Dimension022,Dimension028,Dimension029]
FEATURE [TechDraw::DrawRichAnno] RichTextAnnotation
  AnnoText = <!DOCTYPE HTML PUBLIC "-//W3C//DTD HTML 4.0//EN" "http://www.w3.org/TR/REC-html40/strict.dtd">\n<html><head><meta name="qrichtext" content="1" /><style type="text/css">\np, li { white-space: pre-wrap; }\n</style></head><body style=" font-family:'Bitstream Vera Sans'; font-size:12pt; font-weight:400; font-style:normal;">\n<p style=" margin-top:0px; margin-bottom:0px; margin-left:0px; margin-right:0px; -qt-block-indent:0; text-indent:0px;"><span style=" font-size:7pt;">1. 3/16&quot; clear polycarbonate construction</span></p>\n<p style=" margin-top:0px; margin-bottom:0px; margin-left:0px; margin-right:0px; -qt-block-indent:0; text-indent:0px;"><span style=" font-size:7pt;">2. PVC pinless hinges</span></p>\n<p style=" margin-top:0px; margin-bottom:0px; margin-left:0px; margin-right:0px; -qt-block-indent:0; text-indent:0px;"><span style=" font-size:7pt;">3. side hinges are on inside of box</span></p>\n<p style=" margin-top:0px; margin-bottom:0px; margin-left:0px; margin-right:0px; -qt-block-indent:0; text-indent:0px;"><span style=" font-size:7pt;">4. top hinge is on outisde of box</span></p>\n<p style=" margin-top:0px; margin-bottom:0px; margin-left:0px; margin-right:0px; -qt-block-indent:0; text-indent:0px;"><span style=" font-size:7pt;">5. Connections glued using WeldOn #40</span></p></body></html>
  LockPosition = false
  MaxWidth = -1
  Rotation = 0
  Scale = 0.9
  ScaleType = 0
  ShowFrame = true
  X = 229.741
  Y = 188.565
FEATURE [TechDraw::DrawPage] Page004  label="assembly"
  KeepUpdated = true
  NextBalloonIndex = 1
  ProjectionType = 0
  Scale = 0.9
  Template = -> Template004
  Views = -> [View,RichTextAnnotation]
FEATURE [TechDraw::DrawRichAnno] RichTextAnnotation001
  AnnoText = <!DOCTYPE HTML PUBLIC "-//W3C//DTD HTML 4.0//EN" "http://www.w3.org/TR/REC-html40/strict.dtd">\n<html><head><meta name="qrichtext" content="1" /><style type="text/css">\np, li { white-space: pre-wrap; }\n</style></head><body style=" font-family:'Bitstream Vera Sans'; font-size:12pt; font-weight:400; font-style:normal;">\n<p style=" margin-top:0px; margin-bottom:0px; margin-left:0px; margin-right:0px; -qt-block-indent:0; text-indent:0px;"><span style=" font-size:7pt;">1. Make two identical side panels</span></p></body></html>
  LockPosition = false
  MaxWidth = -1
  Rotation = 0
  ScaleType = 0
  ShowFrame = true
  X = 237.18
  Y = 192.072
FEATURE [TechDraw::DrawPage] Page001  label="side"
  KeepUpdated = true
  NextBalloonIndex = 1
  ProjectionType = 0
  Template = -> Template001
  Views = -> [ProjGroup001,Dimension006,Dimension007,Dimension008,Dimension009,Dimension010,Dimension011,Dimension012,Dimension013,RichTextAnnotation001]
FEATURE [TechDraw::DrawRichAnno] RichTextAnnotation002
  AnnoText = <!DOCTYPE HTML PUBLIC "-//W3C//DTD HTML 4.0//EN" "http://www.w3.org/TR/REC-html40/strict.dtd">\n<html><head><meta name="qrichtext" content="1" /><style type="text/css">\np, li { white-space: pre-wrap; }\n</style></head><body style=" font-family:'Bitstream Vera Sans'; font-size:12pt; font-weight:400; font-style:normal;">\n<p style=" margin-top:0px; margin-bottom:0px; margin-left:0px; margin-right:0px; -qt-block-indent:0; text-indent:0px;"><span style=" font-size:7pt;">1. Make two identical flanges.</span></p>\n<p style=" margin-top:0px; margin-bottom:0px; margin-left:0px; margin-right:0px; -qt-block-indent:0; text-indent:0px;"><span style=" font-size:7pt;">2. Construct each flange from 2 rings glued together or mill a single piece</span></p></body></html>
  LockPosition = false
  MaxWidth = 100
  Rotation = 0
  ScaleType = 0
  ShowFrame = true
  X = 214.892
  Y = 188.573
FEATURE [TechDraw::DrawPage] Page003  label="glove_flange"
  KeepUpdated = true
  NextBalloonIndex = 1
  ProjectionType = 0
  Template = -> Template003
  Views = -> [ProjGroup003,Dimension023,Dimension024,Dimension025,Dimension026,Dimension027,RichTextAnnotation002]
FEATURE [App::DocumentObjectGroup] Group  label="drawings"
  Group = -> [Page004,Page,Page001,Page002,Page003]
FEATURE [Part::Part2DObjectPython] Shape2DView001  label="side_panel_2D"  # Draft 2D object (typed FeaturePython)
  Base = -> Body001
  FuseArch = false
  HiddenLines = false
  InPlace = true
  Placement = pos=(0,0,0) rot=(0,0,1;3.14159rad)
  Projection = (-1,-2.61867e-08,8.42937e-08)
  ProjectionMode = 0
  SegmentLength = 0.05
  Tessellation = false
  VisibleOnly = false
FEATURE [Sketcher::SketchObject] Sketch006
  sketch-geometry (6):
    g0: LineSegment StartX=0 StartY=0 StartZ=0 EndX=502.388 EndY=0 EndZ=0
    g1: LineSegment StartX=502.388 StartY=0 StartZ=0 EndX=502.388 EndY=289.875 EndZ=0
    g2: LineSegment StartX=502.388 StartY=289.875 StartZ=0 EndX=0 EndY=289.875 EndZ=0
    g3: LineSegment StartX=0 StartY=289.875 StartZ=0 EndX=0 EndY=0 EndZ=0
    g4: Circle CenterX=184.15 CenterY=266.7 CenterZ=0 NormalX=0 NormalY=0 NormalZ=1 AngleXU=0 Radius=3.175
    g5: Circle CenterX=476.25 CenterY=262.696 CenterZ=0 NormalX=0 NormalY=0 NormalZ=1 AngleXU=0 Radius=3.175
  constraints (14):
    c: Coincident(g0,g1)
    c: Coincident(g1,g2)
    c: Coincident(g2,g3)
    c: Coincident(g3,g0)
    c: Horizontal(g0)
    c: Horizontal(g2)
    c: Vertical(g1)
    c: Vertical(g3)
    c: Coincident(g0,g-1)
    c: DistanceX(g0,g4) = 184.15
    c: DistanceX(g4,g5) = 292.1
    c: DistanceY(g0,g4) = 266.7
    c: Radius(g4) = 3.175
    c: Radius(g5) = 3.175
